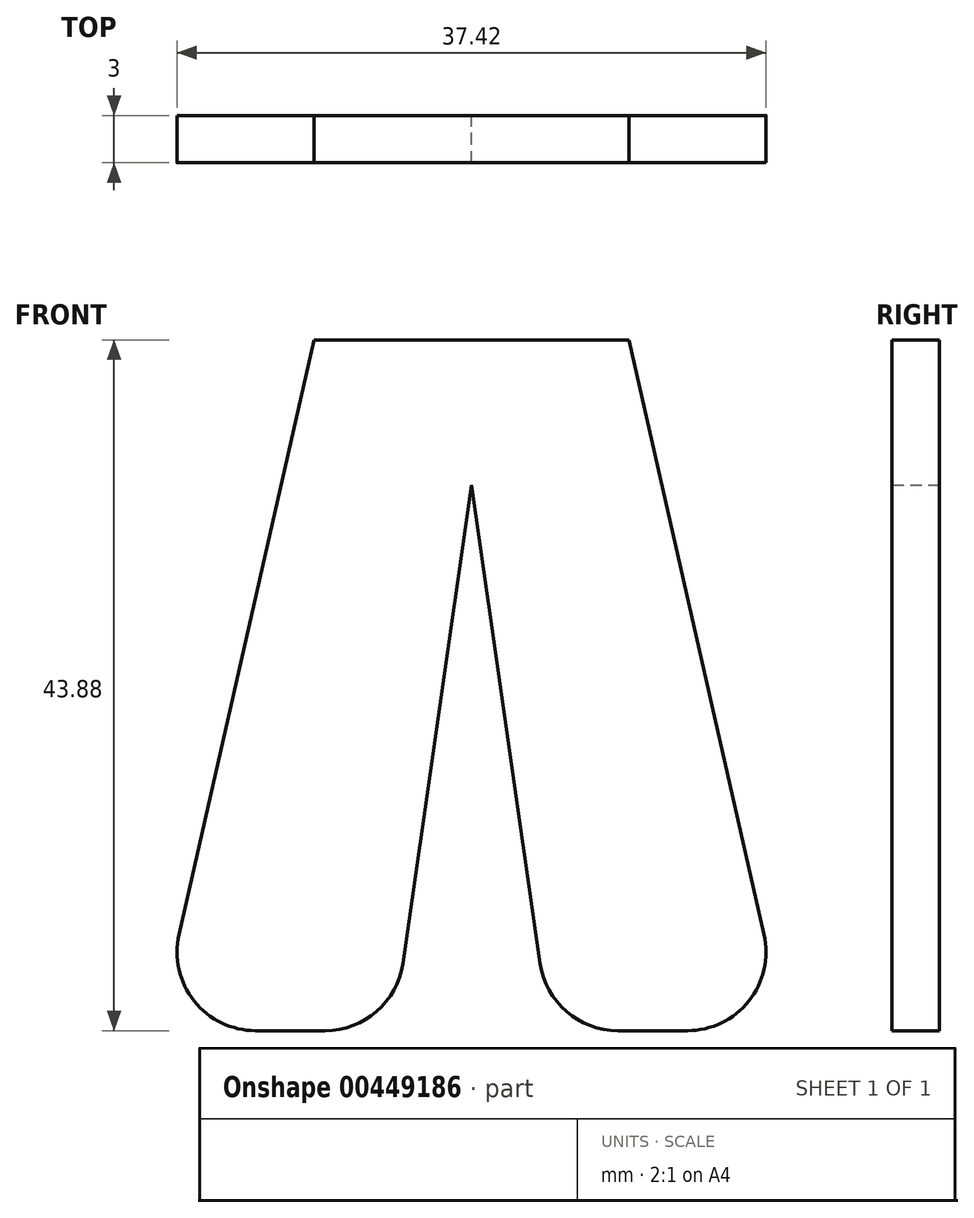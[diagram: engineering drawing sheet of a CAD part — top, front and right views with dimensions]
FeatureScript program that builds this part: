
annotation { "Feature Type Name" : "Feature", "Feature Type Description" : "" }
export const myFeature = defineFeature(function(context is Context, id is Id, definition is map)
    precondition{}
    {
        {
            var Q0;
            Q0=qCreatedBy(makeId("Front.planeOp"),FACE);
            var sketch = newSketch(context, id + "F0", { "sketchPlane" : qUnion([Q0])});
            skLineSegment(sketch, "E0", {"start": v(0, 0) * mm, "end": v(20, 0) * mm});
            skLineSegment(sketch, "E1", {"start": v(20, 0) * mm, "end": v(29.97, -43.88) * mm});
            skLineSegment(sketch, "E2", {"start": v(29.97, -43.88) * mm, "end": v(14.97, -43.88) * mm});
            skLineSegment(sketch, "E3", {"start": v(14.97, -43.88) * mm, "end": v(10, -9.24) * mm});
            skLineSegment(sketch, "E4", {"start": v(10, -9.24) * mm, "end": v(5.03, -43.88) * mm});
            skLineSegment(sketch, "E5", {"start": v(-9.97, -43.88) * mm, "end": v(5.03, -43.88) * mm});
            skLineSegment(sketch, "E6", {"start": v(-9.97, -43.88) * mm, "end": v(0, 0) * mm});
            skLineSegment(sketch, "E7", {"start": v(10, -9.24) * mm, "end": v(21.72, -7.56) * mm});
            skSolve(sketch);
        }
        {
            var Q0;
            Q0 = qSketchRegion(id + "F0", true);
            extrude(context, id + "F1", {"entities" : qUnion([Q0]), "depth" : 3 * mm});
        }
        {
            var Q0;
            Q0=makeQuery(id+"F1.opExtrude","SWEPT_EDGE",EDGE,{"disambiguationData":[OSD([sQuery(id+"F0.wireOp",EDGE,"E5"),sQuery(id+"F0.wireOp",EDGE,"E6")])]});
            var Q1;
            Q1=makeQuery(id+"F1.opExtrude","SWEPT_EDGE",EDGE,{"disambiguationData":[OSD([sQuery(id+"F0.wireOp",EDGE,"E4"),sQuery(id+"F0.wireOp",EDGE,"E5")])]});
            var Q2;
            Q2=makeQuery(id+"F1.opExtrude","SWEPT_EDGE",EDGE,{"disambiguationData":[OSD([sQuery(id+"F0.wireOp",EDGE,"E2"),sQuery(id+"F0.wireOp",EDGE,"E3")])]});
            var Q3;
            Q3=makeQuery(id+"F1.opExtrude","SWEPT_EDGE",EDGE,{"disambiguationData":[OSD([sQuery(id+"F0.wireOp",EDGE,"E1"),sQuery(id+"F0.wireOp",EDGE,"E2")])]});
            fillet(context, id + "F2", {"entities" : qUnion([Q0, Q1, Q2, Q3]), "radius" : 5 * mm, "tangentPropagation" : true, "allowEdgeOverflow" : false});
        }
        {
            var Q0;
            Q0=makeQuery(id+"F1.opExtrude","CAP_FACE",FACE,{"disambiguationData":[OSD([sQuery(id+"F0.wireOp",EDGE,"E0"),sQuery(id+"F0.wireOp",EDGE,"E1"),sQuery(id+"F0.wireOp",EDGE,"E2"),sQuery(id+"F0.wireOp",EDGE,"E3"),sQuery(id+"F0.wireOp",EDGE,"E4"),sQuery(id+"F0.wireOp",EDGE,"E5"),sQuery(id+"F0.wireOp",EDGE,"E6")])],"isStart":false});
            var sketch = newSketch(context, id + "F3", { "sketchPlane" : qUnion([Q0])});
            skSolve(sketch);
        }
    });
